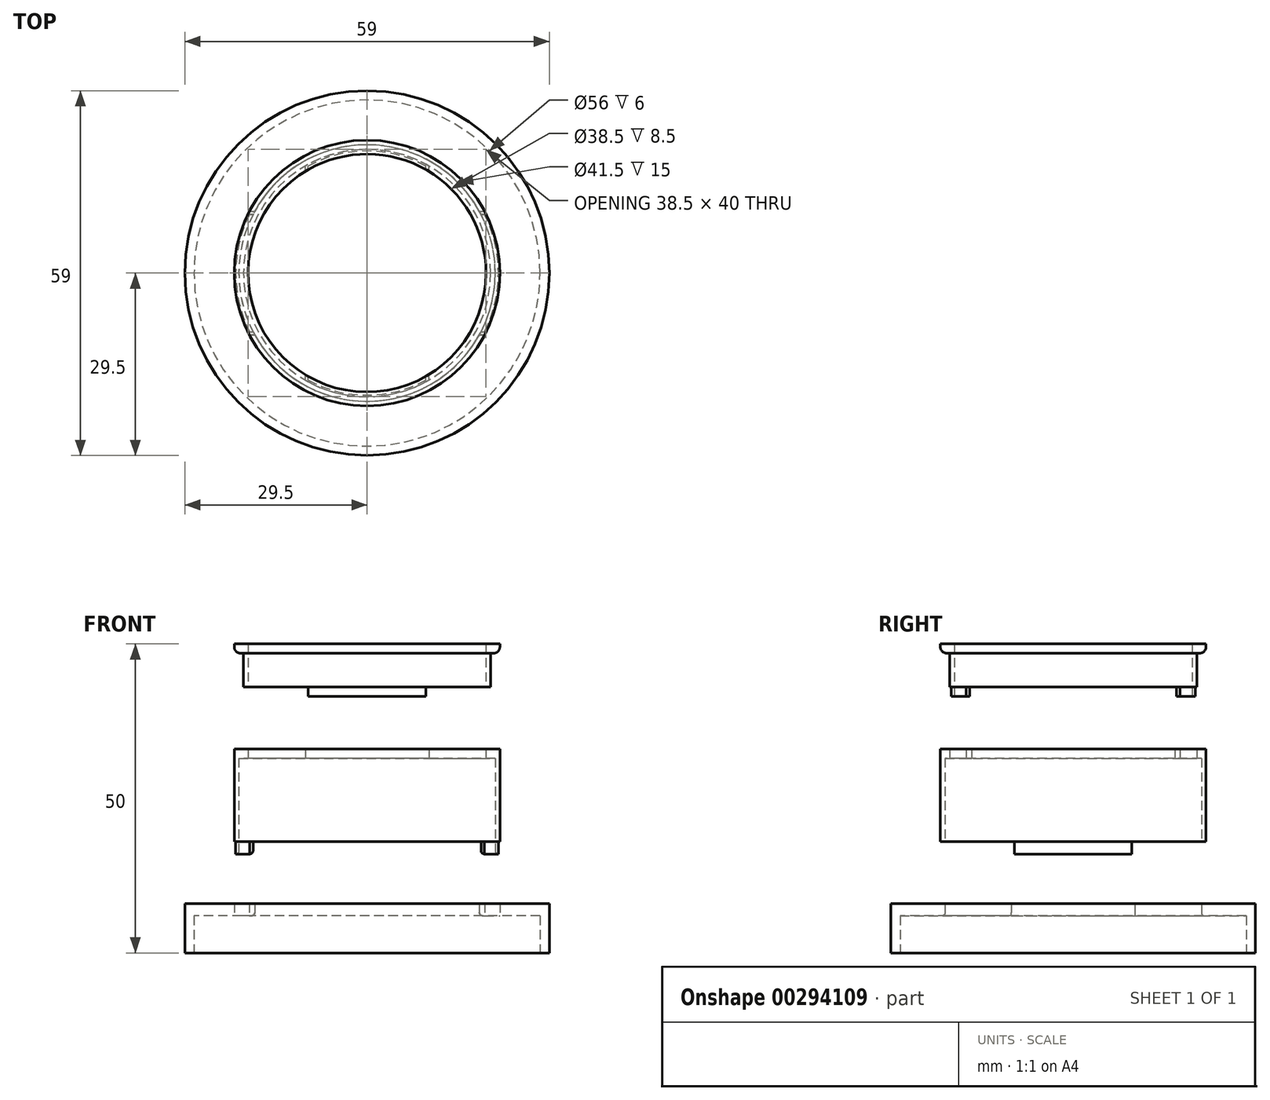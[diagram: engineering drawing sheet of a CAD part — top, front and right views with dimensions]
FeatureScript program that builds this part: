
annotation { "Feature Type Name" : "Feature", "Feature Type Description" : "" }
export const myFeature = defineFeature(function(context is Context, id is Id, definition is map)
    precondition{}
    {
        {
            var Q0;
            Q0=qCreatedBy(makeId("Top.planeOp"),FACE);
            var sketch = newSketch(context, id + "F0", { "sketchPlane" : qUnion([Q0])});
            skCircle(sketch, "E0", {"center": v(0, 0) * mm, "radius": 28 * mm});
            skSolve(sketch);
        }
        {
            var Q0;
            Q0=qCreatedBy(makeId("Top.planeOp"),FACE);
            var sketch = newSketch(context, id + "F1", { "sketchPlane" : qUnion([Q0])});
            skCircle(sketch, "E1", {"center": v(0, 0) * mm, "radius": 29.5 * mm});
            skSolve(sketch);
        }
        {
            var Q0;
            Q0 = qSketchRegion(id + "F1", true);
            extrude(context, id + "F2", {"entities" : qUnion([Q0]), "depth" : 8 * mm});
        }
        {
            var Q0;
            Q0 = qSketchRegion(id + "F0", true);
            extrude(context, id + "F3", {"entities" : qUnion([Q0]), "operationType" : NewBodyOperationType.REMOVE, "depth" : 6 * mm});
        }
        {
            var Q0;
            Q0=makeQuery(id+"F2.opExtrude","CAP_FACE",FACE,{"disambiguationData":[OSD([sQuery(id+"F1.wireOp",EDGE,"E1")])],"isStart":false});
            var sketch = newSketch(context, id + "F4", { "sketchPlane" : qUnion([Q0])});
            skCircle(sketch, "E2", {"center": v(0, 0) * mm, "radius": 21.5 * mm});
            skSolve(sketch);
        }
        {
            var Q0;
            Q0 = qSketchRegion(id + "F4", true);
            var Q1;
            Q1=makeQuery(id+"F4.imprint","IMPRINT",FACE,{"disambiguationData":[TD([[makeQuery(id+"F4.imprint","IMPRINT",EDGE,{"derivedFrom":sQuery(id+"F4.wireOp",EDGE,"E2")}),1.0]])]});
            extrude(context, id + "F5", {"entities" : qUnion([Q0, Q1]), "depth" : 15 * mm});
        }
        {
            var Q0;
            Q0=qCreatedBy(makeId("Top.planeOp"),FACE);
            var sketch = newSketch(context, id + "F6", { "sketchPlane" : qUnion([Q0])});
            skCircle(sketch, "E3", {"center": v(0, 0) * mm, "radius": 20.75 * mm});
            skSolve(sketch);
        }
        {
            var Q0;
            Q0=makeQuery(id+"F6.imprint","IMPRINT",FACE,{"disambiguationData":[TD([[makeQuery(id+"F6.imprint","IMPRINT",EDGE,{"derivedFrom":sQuery(id+"F6.wireOp",EDGE,"E3")}),1.0]])]});
            extrude(context, id + "F7", {"entities" : qUnion([Q0]), "operationType" : NewBodyOperationType.REMOVE, "depth" : 21.5 * mm});
        }
        {
            var Q0;
            Q0=makeQuery(id+"F5.opExtrude","CAP_FACE",FACE,{"disambiguationData":[OSD([sQuery(id+"F4.wireOp",EDGE,"E2")])],"isStart":false});
            var sketch = newSketch(context, id + "F8", { "sketchPlane" : qUnion([Q0])});
            skCircle(sketch, "E4", {"center": v(0, 0) * mm, "radius": 20 * mm});
            skSolve(sketch);
        }
        {
            var Q0;
            Q0 = qSketchRegion(id + "F8", true);
            extrude(context, id + "F9", {"entities" : qUnion([Q0]), "depth" : 7 * mm});
        }
        {
            var Q0;
            Q0=qCreatedBy(makeId("Top.planeOp"),FACE);
            var sketch = newSketch(context, id + "F10", { "sketchPlane" : qUnion([Q0])});
            skCircle(sketch, "E5", {"center": v(0, 0) * mm, "radius": 19.25 * mm});
            skSolve(sketch);
        }
        {
            var Q0;
            Q0=makeQuery(id+"F7.boolean.opBoolean","COPY",FACE,{"derivedFrom":makeQuery(id+"F7.opExtrude","CAP_FACE",FACE,{"disambiguationData":[OSD([sQuery(id+"F6.wireOp",EDGE,"E3")])],"isStart":false})});
            var sketch = newSketch(context, id + "F11", { "sketchPlane" : qUnion([Q0])});
            skLineSegment(sketch, "E6.bottom", {"start": v(-10, 38.1) * mm, "end": v(10, 38.1) * mm});
            skLineSegment(sketch, "E6.top", {"start": v(-10, -33.7) * mm, "end": v(10, -33.7) * mm});
            skLineSegment(sketch, "E6.left", {"start": v(-10, 38.1) * mm, "end": v(-10, -33.7) * mm});
            skLineSegment(sketch, "E6.right", {"start": v(10, 38.1) * mm, "end": v(10, -33.7) * mm});
            skCircle(sketch, "E7", {"center": v(0, 0) * mm, "radius": 20 * mm});
            skSolve(sketch);
        }
        {
            var Q0;
            {var subQ0=sQuery(id+"F11.wireOp",EDGE,"E7");var subQ1=sQuery(id+"F11.wireOp",EDGE,"E6.left");var subQ2=makeQuery(id+"F11.imprint","INTERSECT",VERTEX,{"disambiguationData":[OD(0.0)],"derivedFrom":[subQ1,subQ0]});Q0=makeQuery(id+"F11.imprint","IMPRINT",FACE,{"disambiguationData":[TD([[makeQuery(id+"F11.imprint","IMPRINT",EDGE,{"disambiguationData":[TD([[subQ2,1.0]])],"derivedFrom":subQ0}),1.0]])]});}
            var Q1;
            {var subQ0=sQuery(id+"F11.wireOp",EDGE,"E7");var subQ1=sQuery(id+"F11.wireOp",EDGE,"E6.left");var subQ2=makeQuery(id+"F11.imprint","INTERSECT",VERTEX,{"disambiguationData":[OD(1.0)],"derivedFrom":[subQ1,subQ0]});Q1=makeQuery(id+"F11.imprint","IMPRINT",FACE,{"disambiguationData":[TD([[makeQuery(id+"F11.imprint","IMPRINT",EDGE,{"disambiguationData":[TD([[subQ2,-1.0]])],"derivedFrom":subQ0}),1.0]])]});}
            extrude(context, id + "F12", {"entities" : qUnion([Q0, Q1]), "operationType" : NewBodyOperationType.REMOVE, "oppositeDirection" : true, "depth" : 1.5 * mm});
        }
        {
            var Q0;
            Q0=makeQuery(id+"F9.opExtrude","CAP_FACE",FACE,{"disambiguationData":[OSD([sQuery(id+"F8.wireOp",EDGE,"E4")])],"isStart":true});
            var sketch = newSketch(context, id + "F13", { "sketchPlane" : qUnion([Q0])});
            skLineSegment(sketch, "E8.bottom", {"start": v(-9.5, 33.25) * mm, "end": v(9.5, 33.25) * mm});
            skLineSegment(sketch, "E8.top", {"start": v(-9.5, -23.02) * mm, "end": v(9.5, -23.02) * mm});
            skLineSegment(sketch, "E8.left", {"start": v(-9.5, 33.25) * mm, "end": v(-9.5, -23.02) * mm});
            skLineSegment(sketch, "E8.right", {"start": v(9.5, 33.25) * mm, "end": v(9.5, -23.02) * mm});
            skCircle(sketch, "E9", {"center": v(0, 0) * mm, "radius": 19.75 * mm});
            skSolve(sketch);
        }
        {
            var Q0;
            {var subQ0=sQuery(id+"F11.wireOp",EDGE,"E7");var subQ1=sQuery(id+"F11.wireOp",EDGE,"E6.left");var subQ2=makeQuery(id+"F11.imprint","INTERSECT",VERTEX,{"disambiguationData":[OD(0.0)],"derivedFrom":[subQ1,subQ0]});Q0=makeQuery(id+"F11.imprint","IMPRINT",FACE,{"disambiguationData":[TD([[makeQuery(id+"F11.imprint","IMPRINT",EDGE,{"disambiguationData":[TD([[subQ2,1.0]])],"derivedFrom":subQ0}),1.0]])]});}
            var Q1;
            {var subQ0=sQuery(id+"F11.wireOp",EDGE,"E7");var subQ1=sQuery(id+"F11.wireOp",EDGE,"E6.left");var subQ2=makeQuery(id+"F11.imprint","INTERSECT",VERTEX,{"disambiguationData":[OD(1.0)],"derivedFrom":[subQ1,subQ0]});Q1=makeQuery(id+"F11.imprint","IMPRINT",FACE,{"disambiguationData":[TD([[makeQuery(id+"F11.imprint","IMPRINT",EDGE,{"disambiguationData":[TD([[subQ2,-1.0]])],"derivedFrom":subQ0}),1.0]])]});}
            extrude(context, id + "F14", {"entities" : qUnion([Q0, Q1]), "operationType" : NewBodyOperationType.REMOVE, "depth" : 2 * mm});
        }
        {
            var Q0;
            {var subQ0=sQuery(id+"F13.wireOp",EDGE,"E9");var subQ1=sQuery(id+"F13.wireOp",EDGE,"E8.left");var subQ2=makeQuery(id+"F13.imprint","INTERSECT",VERTEX,{"disambiguationData":[OD(0.0)],"derivedFrom":[subQ1,subQ0]});Q0=makeQuery(id+"F13.imprint","IMPRINT",FACE,{"disambiguationData":[TD([[makeQuery(id+"F13.imprint","IMPRINT",EDGE,{"disambiguationData":[TD([[subQ2,1.0]])],"derivedFrom":subQ0}),1.0]])]});}
            var Q1;
            {var subQ0=sQuery(id+"F13.wireOp",EDGE,"E9");var subQ1=sQuery(id+"F13.wireOp",EDGE,"E8.left");var subQ2=makeQuery(id+"F13.imprint","INTERSECT",VERTEX,{"disambiguationData":[OD(1.0)],"derivedFrom":[subQ1,subQ0]});Q1=makeQuery(id+"F13.imprint","IMPRINT",FACE,{"disambiguationData":[TD([[makeQuery(id+"F13.imprint","IMPRINT",EDGE,{"disambiguationData":[TD([[subQ2,-1.0]])],"derivedFrom":subQ0}),1.0]])]});}
            extrude(context, id + "F15", {"entities" : qUnion([Q0, Q1]), "operationType" : NewBodyOperationType.ADD, "depth" : 1.5 * mm});
        }
        {
            var Q0;
            Q0=makeQuery(id+"F3.boolean.opBoolean","COPY",FACE,{"derivedFrom":makeQuery(id+"F3.opExtrude","CAP_FACE",FACE,{"disambiguationData":[OSD([sQuery(id+"F0.wireOp",EDGE,"E0")])],"isStart":false})});
            var sketch = newSketch(context, id + "F16", { "sketchPlane" : qUnion([Q0])});
            skLineSegment(sketch, "E10.bottom", {"start": v(-44.73, 10) * mm, "end": v(50.7, 10) * mm});
            skLineSegment(sketch, "E10.top", {"start": v(-44.73, -10) * mm, "end": v(50.7, -10) * mm});
            skLineSegment(sketch, "E10.left", {"start": v(-44.73, 10) * mm, "end": v(-44.73, -10) * mm});
            skLineSegment(sketch, "E10.right", {"start": v(50.7, 10) * mm, "end": v(50.7, -10) * mm});
            skCircle(sketch, "E11", {"center": v(0, 0) * mm, "radius": 21.5 * mm});
            skSolve(sketch);
        }
        {
            var Q0;
            {var subQ0=sQuery(id+"F16.wireOp",EDGE,"E11");var subQ1=sQuery(id+"F16.wireOp",EDGE,"E10.bottom");var subQ2=makeQuery(id+"F16.imprint","INTERSECT",VERTEX,{"disambiguationData":[OD(0.0)],"derivedFrom":[subQ1,subQ0]});Q0=makeQuery(id+"F16.imprint","IMPRINT",FACE,{"disambiguationData":[TD([[makeQuery(id+"F16.imprint","IMPRINT",EDGE,{"disambiguationData":[TD([[subQ2,-1.0]])],"derivedFrom":subQ0}),1.0]])]});}
            var Q1;
            {var subQ0=sQuery(id+"F16.wireOp",EDGE,"E11");var subQ1=sQuery(id+"F16.wireOp",EDGE,"E10.bottom");var subQ2=makeQuery(id+"F16.imprint","INTERSECT",VERTEX,{"disambiguationData":[OD(1.0)],"derivedFrom":[subQ1,subQ0]});Q1=makeQuery(id+"F16.imprint","IMPRINT",FACE,{"disambiguationData":[TD([[makeQuery(id+"F16.imprint","IMPRINT",EDGE,{"disambiguationData":[TD([[subQ2,1.0]])],"derivedFrom":subQ0}),1.0]])]});}
            extrude(context, id + "F17", {"entities" : qUnion([Q0, Q1]), "operationType" : NewBodyOperationType.REMOVE, "oppositeDirection" : true, "depth" : 2 * mm});
        }
        {
            var Q0;
            Q0=makeQuery(id+"F5.opExtrude","CAP_FACE",FACE,{"disambiguationData":[OSD([sQuery(id+"F4.wireOp",EDGE,"E2")])],"isStart":true});
            var sketch = newSketch(context, id + "F18", { "sketchPlane" : qUnion([Q0])});
            skLineSegment(sketch, "E12.bottom", {"start": v(-38.6, 9.5) * mm, "end": v(47.83, 9.5) * mm});
            skLineSegment(sketch, "E12.top", {"start": v(-38.6, -9.5) * mm, "end": v(47.83, -9.5) * mm});
            skLineSegment(sketch, "E12.left", {"start": v(-38.6, 9.5) * mm, "end": v(-38.6, -9.5) * mm});
            skLineSegment(sketch, "E12.right", {"start": v(47.83, 9.5) * mm, "end": v(47.83, -9.5) * mm});
            skCircle(sketch, "E13", {"center": v(0, 0) * mm, "radius": 21.25 * mm});
            skSolve(sketch);
        }
        {
            var Q0;
            {var subQ0=sQuery(id+"F18.wireOp",EDGE,"E13");var subQ1=sQuery(id+"F18.wireOp",EDGE,"E12.bottom");var subQ2=makeQuery(id+"F18.imprint","INTERSECT",VERTEX,{"disambiguationData":[OD(0.0)],"derivedFrom":[subQ1,subQ0]});Q0=makeQuery(id+"F18.imprint","IMPRINT",FACE,{"disambiguationData":[TD([[makeQuery(id+"F18.imprint","IMPRINT",EDGE,{"disambiguationData":[TD([[subQ2,-1.0]])],"derivedFrom":subQ0}),1.0]])]});}
            var Q1;
            {var subQ0=sQuery(id+"F18.wireOp",EDGE,"E13");var subQ1=sQuery(id+"F18.wireOp",EDGE,"E12.bottom");var subQ2=makeQuery(id+"F18.imprint","INTERSECT",VERTEX,{"disambiguationData":[OD(1.0)],"derivedFrom":[subQ1,subQ0]});Q1=makeQuery(id+"F18.imprint","IMPRINT",FACE,{"disambiguationData":[TD([[makeQuery(id+"F18.imprint","IMPRINT",EDGE,{"disambiguationData":[TD([[subQ2,1.0]])],"derivedFrom":subQ0}),1.0]])]});}
            extrude(context, id + "F19", {"entities" : qUnion([Q0, Q1]), "operationType" : NewBodyOperationType.ADD, "depth" : 2 * mm});
        }
        {
            var Q0;
            Q0=makeQuery(id+"F3.boolean.opBoolean","COPY",EDGE,{"derivedFrom":makeQuery(id+"F3.opExtrude","CAP_EDGE",EDGE,{"disambiguationData":[OSD([sQuery(id+"F0.wireOp",EDGE,"E0")])],"isStart":true})});
            var Q1;
            {var subQ0=makeQuery(id+"F3.boolean.opBoolean","COPY",FACE,{"derivedFrom":makeQuery(id+"F3.opExtrude","CAP_FACE",FACE,{"disambiguationData":[OSD([sQuery(id+"F0.wireOp",EDGE,"E0")])],"isStart":false})});var subQ1=makeQuery(id+"F7.opExtrude","SWEPT_FACE",FACE,{"disambiguationData":[OSD([sQuery(id+"F6.wireOp",EDGE,"E3")])]});var subQ2=sQuery(id+"F16.wireOp",EDGE,"E11");var subQ3=sQuery(id+"F16.wireOp",EDGE,"E10.bottom");var subQ4=makeQuery(id+"F7.boolean.opBoolean","INTERSECT",EDGE,{"derivedFrom":[subQ0,subQ1]});Q1=makeQuery(id+"F17.boolean.opBoolean","SPLIT",EDGE,{"disambiguationData":[TD([makeQuery(id+"F17.opExtrude","SWEPT_FACE",FACE,{"disambiguationData":[OSD([subQ3]),TDD([makeQuery(id+"F16.imprint","IMPRINT",EDGE,{"disambiguationData":[TD([[makeQuery(id+"F16.imprint","INTERSECT",VERTEX,{"disambiguationData":[OD(0.0)],"derivedFrom":[subQ3,subQ2]}),-1.0]])],"derivedFrom":subQ3})])]})])],"derivedFrom":subQ4});}
            var Q2;
            {var subQ0=sQuery(id+"F6.wireOp",EDGE,"E3");var subQ1=sQuery(id+"F4.wireOp",EDGE,"E2");var subQ2=makeQuery(id+"F7.boolean.opBoolean","INTERSECT",EDGE,{"derivedFrom":[makeQuery(id+"F5.opExtrude","CAP_FACE",FACE,{"disambiguationData":[OSD([subQ1])],"isStart":true}),makeQuery(id+"F7.opExtrude","SWEPT_FACE",FACE,{"disambiguationData":[OSD([subQ0])]})]});Q2=makeQuery(id+"F19.opExtrude","CAP_EDGE",EDGE,{"disambiguationData":[OSD([subQ1,subQ0]),TDD([makeQuery(id+"F18.imprint","IMPRINT",EDGE,{"disambiguationData":[TD([[makeQuery(id+"F18.imprint","INTERSECT",VERTEX,{"disambiguationData":[OD(1.0)],"derivedFrom":[subQ2,sQuery(id+"F18.wireOp",EDGE,"E12.bottom")]}),1.0]])],"derivedFrom":subQ2})])],"isStart":false});}
            var Q3;
            {var subQ0=sQuery(id+"F6.wireOp",EDGE,"E3");var subQ1=sQuery(id+"F4.wireOp",EDGE,"E2");var subQ2=makeQuery(id+"F7.boolean.opBoolean","INTERSECT",EDGE,{"derivedFrom":[makeQuery(id+"F5.opExtrude","CAP_FACE",FACE,{"disambiguationData":[OSD([subQ1])],"isStart":true}),makeQuery(id+"F7.opExtrude","SWEPT_FACE",FACE,{"disambiguationData":[OSD([subQ0])]})]});Q3=makeQuery(id+"F19.opExtrude","CAP_EDGE",EDGE,{"disambiguationData":[OSD([subQ1,subQ0]),TDD([makeQuery(id+"F18.imprint","IMPRINT",EDGE,{"disambiguationData":[TD([[makeQuery(id+"F18.imprint","INTERSECT",VERTEX,{"disambiguationData":[OD(0.0)],"derivedFrom":[subQ2,sQuery(id+"F18.wireOp",EDGE,"E12.bottom")]}),-1.0]])],"derivedFrom":subQ2})])],"isStart":false});}
            var Q4;
            {var subQ0=sQuery(id+"F10.wireOp",EDGE,"E5");var subQ1=sQuery(id+"F8.wireOp",EDGE,"E4");var subQ2=makeQuery(id+"F23.boolean.opBoolean","INTERSECT",EDGE,{"derivedFrom":[makeQuery(id+"F9.opExtrude","CAP_FACE",FACE,{"disambiguationData":[OSD([subQ1])],"isStart":true}),makeQuery(id+"F23.opExtrude","SWEPT_FACE",FACE,{"disambiguationData":[OSD([subQ0])]})]});Q4=makeQuery(id+"F15.opExtrude","CAP_EDGE",EDGE,{"disambiguationData":[OSD([subQ1,subQ0]),TDD([makeQuery(id+"F13.imprint","IMPRINT",EDGE,{"disambiguationData":[TD([[makeQuery(id+"F13.imprint","INTERSECT",VERTEX,{"disambiguationData":[OD(0.0)],"derivedFrom":[subQ2,sQuery(id+"F13.wireOp",EDGE,"E8.left")]}),1.0]])],"derivedFrom":subQ2})])],"isStart":false});}
            var Q5;
            {var subQ0=sQuery(id+"F6.wireOp",EDGE,"E3");var subQ1=makeQuery(id+"F7.boolean.opBoolean","COPY",FACE,{"derivedFrom":makeQuery(id+"F7.opExtrude","CAP_FACE",FACE,{"disambiguationData":[OSD([subQ0])],"isStart":false})});var subQ2=sQuery(id+"F11.wireOp",EDGE,"E6.left");var subQ3=makeQuery(id+"F7.boolean.opBoolean","COPY",EDGE,{"derivedFrom":makeQuery(id+"F7.opExtrude","CAP_EDGE",EDGE,{"disambiguationData":[OSD([subQ0])],"isStart":false})});var subQ4=makeQuery(id+"F23.opExtrude","SWEPT_FACE",FACE,{"disambiguationData":[OSD([sQuery(id+"F10.wireOp",EDGE,"E5")])]});var subQ5=makeQuery(id+"F23.boolean.opBoolean","INTERSECT",EDGE,{"derivedFrom":[subQ1,subQ4]});Q5=makeQuery(id+"F14.boolean.opBoolean","SPLIT",EDGE,{"disambiguationData":[TD([makeQuery(id+"F14.opExtrude","SWEPT_FACE",FACE,{"disambiguationData":[OSD([subQ2]),TDD([makeQuery(id+"F11.imprint","IMPRINT",EDGE,{"disambiguationData":[TD([[makeQuery(id+"F11.imprint","INTERSECT",VERTEX,{"disambiguationData":[OD(0.0)],"derivedFrom":[subQ3,subQ2]}),-1.0]])],"derivedFrom":subQ2})])]})])],"derivedFrom":subQ5});}
            var Q6;
            {var subQ0=sQuery(id+"F6.wireOp",EDGE,"E3");var subQ1=makeQuery(id+"F7.boolean.opBoolean","COPY",FACE,{"derivedFrom":makeQuery(id+"F7.opExtrude","CAP_FACE",FACE,{"disambiguationData":[OSD([subQ0])],"isStart":false})});var subQ2=makeQuery(id+"F23.opExtrude","SWEPT_FACE",FACE,{"disambiguationData":[OSD([sQuery(id+"F10.wireOp",EDGE,"E5")])]});var subQ3=sQuery(id+"F11.wireOp",EDGE,"E6.right");var subQ4=makeQuery(id+"F7.boolean.opBoolean","COPY",EDGE,{"derivedFrom":makeQuery(id+"F7.opExtrude","CAP_EDGE",EDGE,{"disambiguationData":[OSD([subQ0])],"isStart":false})});var subQ5=makeQuery(id+"F23.boolean.opBoolean","INTERSECT",EDGE,{"derivedFrom":[subQ1,subQ2]});Q6=makeQuery(id+"F14.boolean.opBoolean","SPLIT",EDGE,{"disambiguationData":[TD([makeQuery(id+"F14.opExtrude","SWEPT_FACE",FACE,{"disambiguationData":[OSD([subQ3]),TDD([makeQuery(id+"F11.imprint","IMPRINT",EDGE,{"disambiguationData":[TD([[makeQuery(id+"F11.imprint","INTERSECT",VERTEX,{"disambiguationData":[OD(0.0)],"derivedFrom":[subQ4,subQ3]}),-1.0]])],"derivedFrom":subQ3})])]})])],"derivedFrom":subQ5});}
            var Q7;
            {var subQ0=makeQuery(id+"F3.boolean.opBoolean","COPY",FACE,{"derivedFrom":makeQuery(id+"F3.opExtrude","CAP_FACE",FACE,{"disambiguationData":[OSD([sQuery(id+"F0.wireOp",EDGE,"E0")])],"isStart":false})});var subQ1=sQuery(id+"F16.wireOp",EDGE,"E11");var subQ2=sQuery(id+"F16.wireOp",EDGE,"E10.top");var subQ3=makeQuery(id+"F7.opExtrude","SWEPT_FACE",FACE,{"disambiguationData":[OSD([sQuery(id+"F6.wireOp",EDGE,"E3")])]});var subQ4=makeQuery(id+"F7.boolean.opBoolean","INTERSECT",EDGE,{"derivedFrom":[subQ0,subQ3]});Q7=makeQuery(id+"F17.boolean.opBoolean","SPLIT",EDGE,{"disambiguationData":[TD([makeQuery(id+"F17.opExtrude","SWEPT_FACE",FACE,{"disambiguationData":[OSD([subQ2]),TDD([makeQuery(id+"F16.imprint","IMPRINT",EDGE,{"disambiguationData":[TD([[makeQuery(id+"F16.imprint","INTERSECT",VERTEX,{"disambiguationData":[OD(0.0)],"derivedFrom":[subQ2,subQ1]}),-1.0]])],"derivedFrom":subQ2})])]})])],"derivedFrom":subQ4});}
            var Q8;
            {var subQ0=sQuery(id+"F10.wireOp",EDGE,"E5");var subQ1=sQuery(id+"F8.wireOp",EDGE,"E4");var subQ2=makeQuery(id+"F23.boolean.opBoolean","INTERSECT",EDGE,{"derivedFrom":[makeQuery(id+"F9.opExtrude","CAP_FACE",FACE,{"disambiguationData":[OSD([subQ1])],"isStart":true}),makeQuery(id+"F23.opExtrude","SWEPT_FACE",FACE,{"disambiguationData":[OSD([subQ0])]})]});Q8=makeQuery(id+"F15.opExtrude","CAP_EDGE",EDGE,{"disambiguationData":[OSD([subQ1,subQ0]),TDD([makeQuery(id+"F13.imprint","IMPRINT",EDGE,{"disambiguationData":[TD([[makeQuery(id+"F13.imprint","INTERSECT",VERTEX,{"disambiguationData":[OD(1.0)],"derivedFrom":[subQ2,sQuery(id+"F13.wireOp",EDGE,"E8.left")]}),-1.0]])],"derivedFrom":subQ2})])],"isStart":false});}
            fillet(context, id + "F20", {"entities" : qUnion([Q0, Q1, Q2, Q3, Q4, Q5, Q6, Q7, Q8]), "radius" : 0.5 * mm, "tangentPropagation" : true, "allowEdgeOverflow" : false});
        }
        {
            var Q0;
            Q0=makeQuery(id+"F9.opExtrude","CAP_FACE",FACE,{"disambiguationData":[OSD([sQuery(id+"F8.wireOp",EDGE,"E4")])],"isStart":false});
            var sketch = newSketch(context, id + "F21", { "sketchPlane" : qUnion([Q0])});
            skCircle(sketch, "E14", {"center": v(0, 0) * mm, "radius": 21.5 * mm});
            skSolve(sketch);
        }
        {
            var Q0;
            Q0=makeQuery(id+"F21.imprint","IMPRINT",FACE,{"disambiguationData":[TD([[makeQuery(id+"F21.imprint","IMPRINT",EDGE,{"derivedFrom":makeQuery(id+"F23.boolean.opBoolean","INTERSECT",EDGE,{"derivedFrom":[makeQuery(id+"F9.opExtrude","CAP_FACE",FACE,{"disambiguationData":[OSD([sQuery(id+"F8.wireOp",EDGE,"E4")])],"isStart":false}),makeQuery(id+"F23.opExtrude","SWEPT_FACE",FACE,{"disambiguationData":[OSD([sQuery(id+"F10.wireOp",EDGE,"E5")])]})]})}),-1.0]])]});
            var Q1;
            Q1 = qSketchRegion(id + "F21", true);
            extrude(context, id + "F22", {"entities" : qUnion([Q0, Q1]), "operationType" : NewBodyOperationType.ADD, "oppositeDirection" : true, "depth" : 1.5 * mm});
        }
        {
            var Q0;
            Q0 = qSketchRegion(id + "F10", true);
            extrude(context, id + "F23", {"entities" : qUnion([Q0]), "operationType" : NewBodyOperationType.REMOVE, "depth" : 50 * mm});
        }
        {
            var Q0;
            Q0=makeQuery(id+"F22.opExtrude","CAP_EDGE",EDGE,{"disambiguationData":[OSD([sQuery(id+"F21.wireOp",EDGE,"E14")])],"isStart":false});
            fillet(context, id + "F24", {"entities" : qUnion([Q0]), "radius" : 1 * mm, "tangentPropagation" : true, "allowEdgeOverflow" : false});
        }
        {
            var Q0;
            Q0=makeQuery(id+"F5.opExtrude","SWEPT_BODY",BODY,{"disambiguationData":[OSD([sQuery(id+"F4.wireOp",EDGE,"E2")])]});
            var Q1;
            Q1=makeQuery(id+"F9.opExtrude","SWEPT_BODY",BODY,{"disambiguationData":[OSD([sQuery(id+"F8.wireOp",EDGE,"E4")])]});
            transform(context, id + "F25", {"entities" : qUnion([Q0, Q1]), "transformType" : TransformType.TRANSLATION_3D, "dx" : 0 * mm, "dy" : 0 * mm, "dz" : 10 * mm, "makeCopy" : false});
        }
        {
            var Q0;
            Q0=makeQuery(id+"F9.opExtrude","SWEPT_BODY",BODY,{"disambiguationData":[OSD([sQuery(id+"F8.wireOp",EDGE,"E4")])]});
            transform(context, id + "F26", {"entities" : qUnion([Q0]), "transformType" : TransformType.TRANSLATION_3D, "dx" : 0 * mm, "dy" : 0 * mm, "dz" : 10 * mm, "makeCopy" : false});
        }
    });
